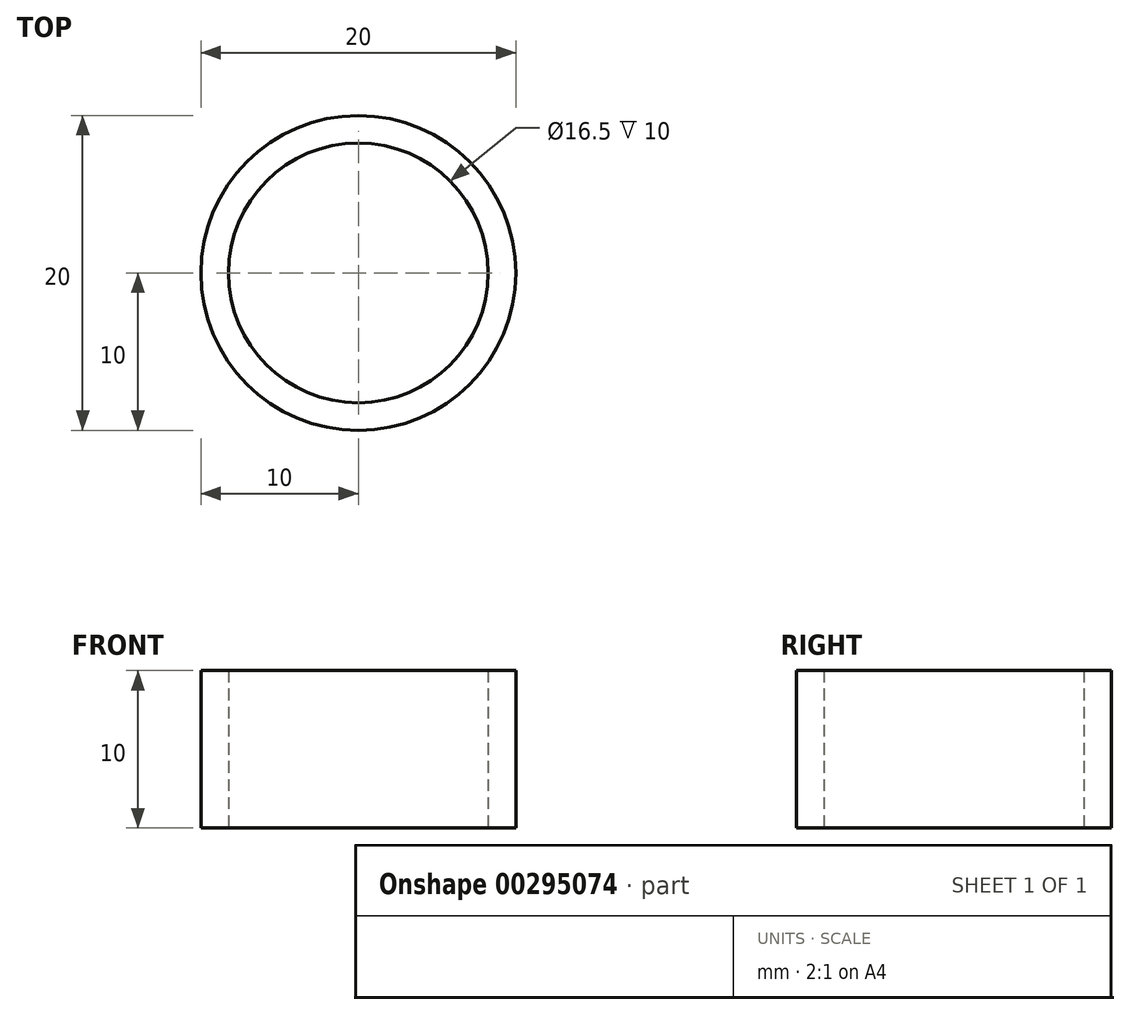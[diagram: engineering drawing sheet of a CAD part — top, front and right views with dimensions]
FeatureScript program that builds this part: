
annotation { "Feature Type Name" : "Feature", "Feature Type Description" : "" }
export const myFeature = defineFeature(function(context is Context, id is Id, definition is map)
    precondition{}
    {
        {
            var Q0;
            Q0=qCreatedBy(makeId("Top.planeOp"),FACE);
            var sketch = newSketch(context, id + "F0", { "sketchPlane" : qUnion([Q0])});
            skCircle(sketch, "E0", {"center": v(0, 0) * mm, "radius": 10 * mm});
            skCircle(sketch, "E1", {"center": v(0, 0) * mm, "radius": 8.25 * mm});
            skSolve(sketch);
        }
        {
            var Q0;
            Q0 = qSketchRegion(id + "F0", true);
            extrude(context, id + "F1", {"entities" : qUnion([Q0]), "depth" : 10 * mm});
        }
    });
